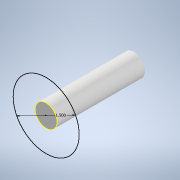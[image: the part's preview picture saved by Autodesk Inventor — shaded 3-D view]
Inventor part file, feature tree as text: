
AUTODESK INVENTOR PART (.ipt)
format: ipt  version: 2021 (Build 250183000, 183)  size: 120,320 bytes
history: native  units: in
note: dims shown in document units (in); Inventor stores cm internally (conversion verified against a paired STEP export)
features: extrude x3, sketch x3
ambient origin geometry x8: Origin, YZ Plane, XZ Plane, XY Plane, X Axis, Y Axis, Z Axis, Center Point
bodies: Solid1 (feature_tree)
feature tree (6):
  extrude  "Extrusion1"  Depth=2.0in TaperAngle=0.0deg
  extrude  "Extrusion2"  Depth=0.25in TaperAngle=0.0deg
  extrude  "Extrusion3"  Depth=1.0in
  sketch  "Sketch1"  dims[d0=0.5in d1=2.0in d2=0.0in]
  sketch  "Sketch2"  dims[d3=1.5in d4=0.25in d5=0.0in]
  sketch  "Sketch4"  dims[d6=0.125in d7=0.125in d8=1.0in d9=0.0in]
